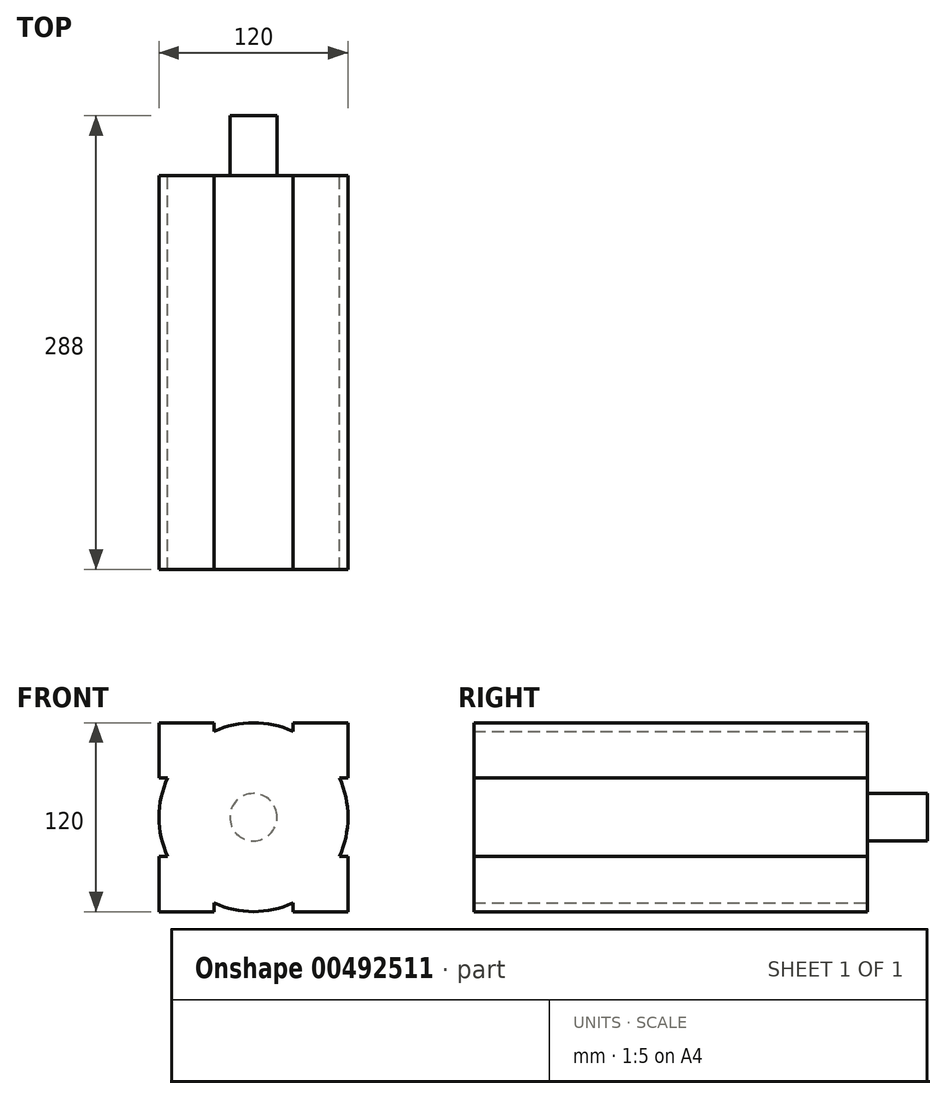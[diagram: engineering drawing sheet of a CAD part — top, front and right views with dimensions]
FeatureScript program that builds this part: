
annotation { "Feature Type Name" : "Feature", "Feature Type Description" : "" }
export const myFeature = defineFeature(function(context is Context, id is Id, definition is map)
    precondition{}
    {
        {
            var Q0;
            Q0=qCreatedBy(makeId("Front.planeOp"),FACE);
            var sketch = newSketch(context, id + "F0", { "sketchPlane" : qUnion([Q0])});
            skArc(sketch, "E0", {"start": v(-54.54, 25) * mm, "mid": v(-60, 0) * mm, "end": v(-54.54, -25) * mm});
            skLineSegment(sketch, "E1.top", {"start": v(-60, 60) * mm, "end": v(-25, 60) * mm});
            skLineSegment(sketch, "E1.left", {"start": v(-60, -60) * mm, "end": v(-60, -25) * mm});
            skLineSegment(sketch, "E1.right", {"start": v(60, -60) * mm, "end": v(60, -25) * mm});
            skLineSegment(sketch, "E2.bottom", {"start": v(-60, -60) * mm, "end": v(-25, -60) * mm});
            skLineSegment(sketch, "E2.right", {"start": v(-25, -60) * mm, "end": v(-25, -54.54) * mm});
            skLineSegment(sketch, "E3.top", {"start": v(-60, 25) * mm, "end": v(-54.54, 25) * mm});
            skLineSegment(sketch, "E3.left", {"start": v(-60, 60) * mm, "end": v(-60, 25) * mm});
            skLineSegment(sketch, "E4.bottom", {"start": v(60, 60) * mm, "end": v(25, 60) * mm});
            skLineSegment(sketch, "E4.top", {"start": v(60, 25) * mm, "end": v(54.54, 25) * mm});
            skLineSegment(sketch, "E4.left", {"start": v(60, 60) * mm, "end": v(60, 25) * mm});
            skLineSegment(sketch, "E4.right", {"start": v(25, 60) * mm, "end": v(25, 54.54) * mm});
            skLineSegment(sketch, "E5.bottom", {"start": v(60, -60) * mm, "end": v(25, -60) * mm});
            skLineSegment(sketch, "E5.top", {"start": v(60, -25) * mm, "end": v(54.54, -25) * mm});
            skLineSegment(sketch, "E6.trimOffspring", {"start": v(-60, 25) * mm, "end": v(-60, 60) * mm});
            skLineSegment(sketch, "E7.trimOffspring", {"start": v(25, -60) * mm, "end": v(60, -60) * mm});
            skLineSegment(sketch, "E8", {"start": v(25, -60) * mm, "end": v(25, -54.54) * mm});
            skLineSegment(sketch, "E9.trimOffspring", {"start": v(60, 25) * mm, "end": v(60, 60) * mm});
            skLineSegment(sketch, "E10.trimOffspring", {"start": v(25, 60) * mm, "end": v(60, 60) * mm});
            skLineSegment(sketch, "E11", {"start": v(-25, 60) * mm, "end": v(-25, 54.54) * mm});
            skLineSegment(sketch, "E12", {"start": v(-60, -25) * mm, "end": v(-54.54, -25) * mm});
            skArc(sketch, "E13.trimOffspring", {"start": v(-25, -54.54) * mm, "mid": v(0, -60) * mm, "end": v(25, -54.54) * mm});
            skArc(sketch, "E14.trimOffspring", {"start": v(54.54, -25) * mm, "mid": v(60, 0) * mm, "end": v(54.54, 25) * mm});
            skArc(sketch, "E15.trimOffspring", {"start": v(25, 54.54) * mm, "mid": v(0, 60) * mm, "end": v(-25, 54.54) * mm});
            skSolve(sketch);
        }
        {
            var Q0;
            Q0=makeQuery(id+"F0.imprint","IMPRINT",FACE,{"disambiguationData":[TD([[makeQuery(id+"F0.imprint","IMPRINT",EDGE,{"derivedFrom":sQuery(id+"F0.wireOp",EDGE,"E0")}),1.0]])]});
            extrude(context, id + "F1", {"entities" : qUnion([Q0]), "depth" : 250 * mm});
        }
        {
            var Q0;
            Q0=makeQuery(id+"F1.opExtrude","CAP_FACE",FACE,{"disambiguationData":[OSD([sQuery(id+"F0.wireOp",EDGE,"E0"),sQuery(id+"F0.wireOp",EDGE,"E2.bottom"),sQuery(id+"F0.wireOp",EDGE,"E1.left"),sQuery(id+"F0.wireOp",EDGE,"E2.right"),sQuery(id+"F0.wireOp",EDGE,"E1.top"),sQuery(id+"F0.wireOp",EDGE,"E3.top"),sQuery(id+"F0.wireOp",EDGE,"E4.top"),sQuery(id+"F0.wireOp",EDGE,"E4.right"),sQuery(id+"F0.wireOp",EDGE,"E5.top"),sQuery(id+"F0.wireOp",EDGE,"E1.right"),sQuery(id+"F0.wireOp",EDGE,"E6.trimOffspring"),sQuery(id+"F0.wireOp",EDGE,"E7.trimOffspring"),sQuery(id+"F0.wireOp",EDGE,"E8"),sQuery(id+"F0.wireOp",EDGE,"E9.trimOffspring"),sQuery(id+"F0.wireOp",EDGE,"E10.trimOffspring"),sQuery(id+"F0.wireOp",EDGE,"E11"),sQuery(id+"F0.wireOp",EDGE,"E12"),sQuery(id+"F0.wireOp",EDGE,"E13.trimOffspring"),sQuery(id+"F0.wireOp",EDGE,"E14.trimOffspring"),sQuery(id+"F0.wireOp",EDGE,"E15.trimOffspring")])],"isStart":true});
            var sketch = newSketch(context, id + "F2", { "sketchPlane" : qUnion([Q0])});
            skCircle(sketch, "E16", {"center": v(0, 0) * mm, "radius": 15 * mm});
            skSolve(sketch);
        }
        {
            var Q0;
            Q0=makeQuery(id+"F2.imprint","IMPRINT",FACE,{"disambiguationData":[TD([[makeQuery(id+"F2.imprint","IMPRINT",EDGE,{"derivedFrom":sQuery(id+"F2.wireOp",EDGE,"E16")}),1.0]])]});
            extrude(context, id + "F3", {"entities" : qUnion([Q0]), "operationType" : NewBodyOperationType.ADD, "depth" : 38 * mm});
        }
    });
